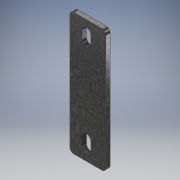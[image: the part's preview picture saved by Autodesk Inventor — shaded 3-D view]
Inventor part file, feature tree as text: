
AUTODESK INVENTOR PART (.ipt)
format: ipt  version: 2017 (Build 210142000, 142)  size: 148,480 bytes
history: native  units: mm
features: extrude x2, sketch x2, other x1, fillet x1
ambient origin geometry x8: Origin, YZ Plane, XZ Plane, XY Plane, X Axis, Y Axis, Z Axis, Center Point
bodies: Body1 (feature_tree)
feature tree (6):
  other  "Sólido1"
  extrude  "Extrusión1"  Depth=41.275mm
  extrude  "Extrusión2"  Depth=10.0mm
  fillet  "Empalme1"  Radius=17.4625mm
  sketch  "Boceto1"  dims[d0=139.7mm d1=41.275mm]
  sketch  "Boceto2"  dims[d2=5.0mm d3=0.0mm d4=10.0mm d5=17.4625mm d6=10.0mm d7=10.0mm d8=19.446875mm d9=19.05mm d10=10.0mm d11=10.0mm d12=10.0mm d13=19.446875mm d14=19.05mm d15=17.4625mm d16=4.365625mm d17=0.0mm d18=4.7625mm]
